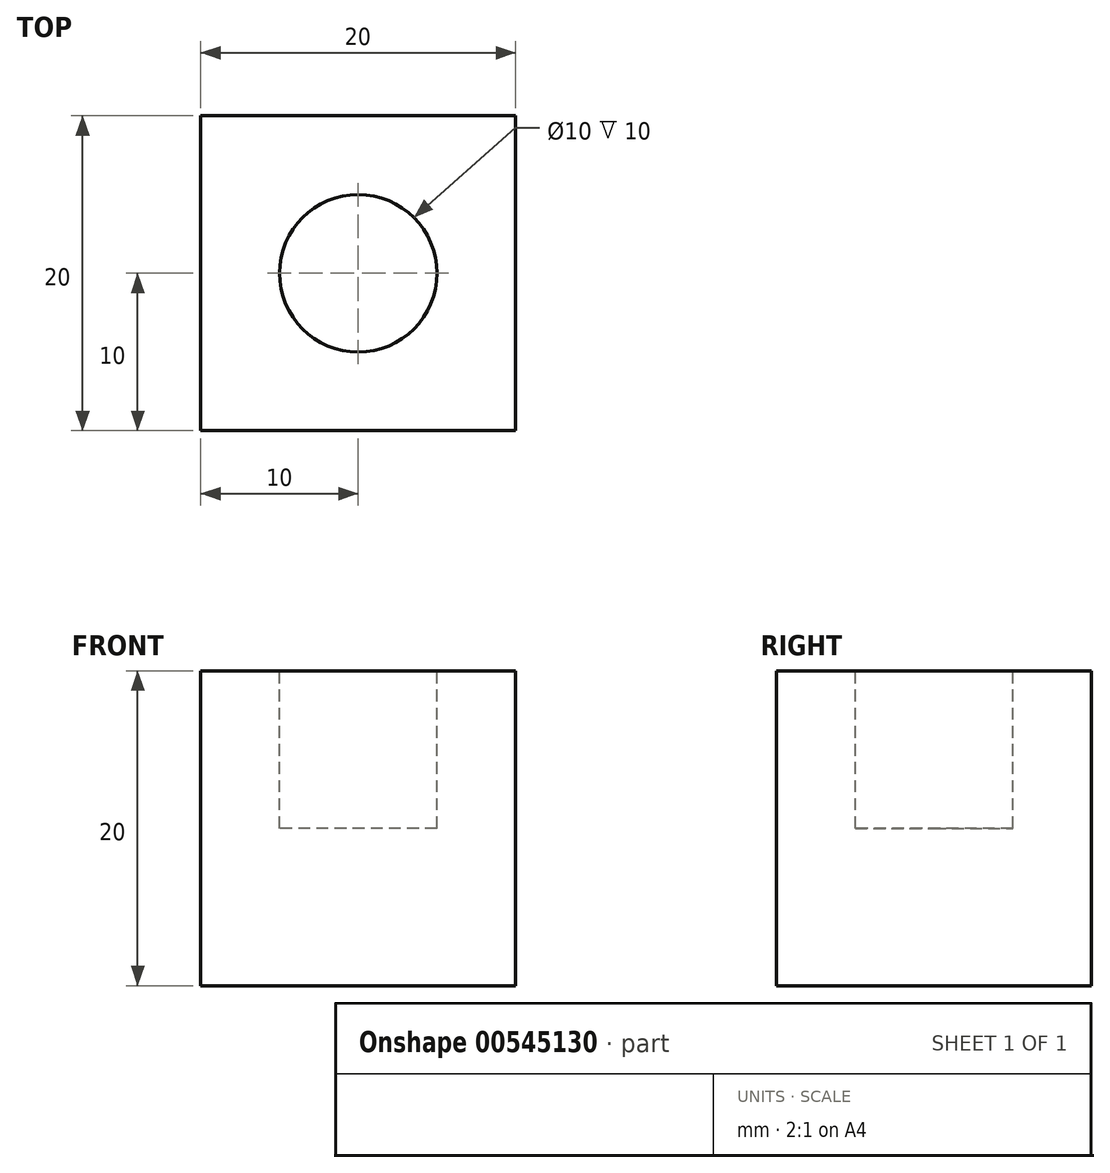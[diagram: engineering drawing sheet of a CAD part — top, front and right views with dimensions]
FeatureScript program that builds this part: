
annotation { "Feature Type Name" : "Feature", "Feature Type Description" : "" }
export const myFeature = defineFeature(function(context is Context, id is Id, definition is map)
    precondition{}
    {
        {
            var Q0;
            Q0=qCreatedBy(makeId("Top.planeOp"),FACE);
            var sketch = newSketch(context, id + "F0", { "sketchPlane" : qUnion([Q0])});
            skLineSegment(sketch, "E0.bottom", {"start": v(0, 0) * mm, "end": v(-20, 0) * mm});
            skLineSegment(sketch, "E0.top", {"start": v(0, 20) * mm, "end": v(-20, 20) * mm});
            skLineSegment(sketch, "E0.left", {"start": v(0, 0) * mm, "end": v(0, 20) * mm});
            skLineSegment(sketch, "E0.right", {"start": v(-20, 0) * mm, "end": v(-20, 20) * mm});
            skSolve(sketch);
        }
        {
            var Q0;
            Q0=makeQuery(id+"F0.imprint","IMPRINT",FACE,{"disambiguationData":[TD([[makeQuery(id+"F0.imprint","IMPRINT",EDGE,{"derivedFrom":sQuery(id+"F0.wireOp",EDGE,"E0.bottom")}),-1.0]])]});
            extrude(context, id + "F1", {"entities" : qUnion([Q0]), "depth" : 20 * mm, "offsetDistance" : 25 * mm});
        }
        {
            var Q0;
            Q0=makeQuery(id+"F1.opExtrude","CAP_FACE",FACE,{"disambiguationData":[OSD([sQuery(id+"F0.wireOp",EDGE,"E0.bottom"),sQuery(id+"F0.wireOp",EDGE,"E0.top"),sQuery(id+"F0.wireOp",EDGE,"E0.left"),sQuery(id+"F0.wireOp",EDGE,"E0.right")])],"isStart":false});
            var sketch = newSketch(context, id + "F2", { "sketchPlane" : qUnion([Q0])});
            skCircle(sketch, "E1", {"center": v(-10, 10) * mm, "radius": 5 * mm});
            skLineSegment(sketch, "E2", {"start": v(-20, 20) * mm, "end": v(0, 0) * mm, "construction": true});
            skLineSegment(sketch, "E3", {"start": v(0, 20) * mm, "end": v(-20, 0) * mm, "construction": true});
            skSolve(sketch);
        }
        {
            var Q0;
            Q0 = qSketchRegion(id + "F2", true);
            extrude(context, id + "F3", {"entities" : qUnion([Q0]), "operationType" : NewBodyOperationType.REMOVE, "oppositeDirection" : true, "depth" : 10 * mm, "offsetDistance" : 25 * mm});
        }
    });
